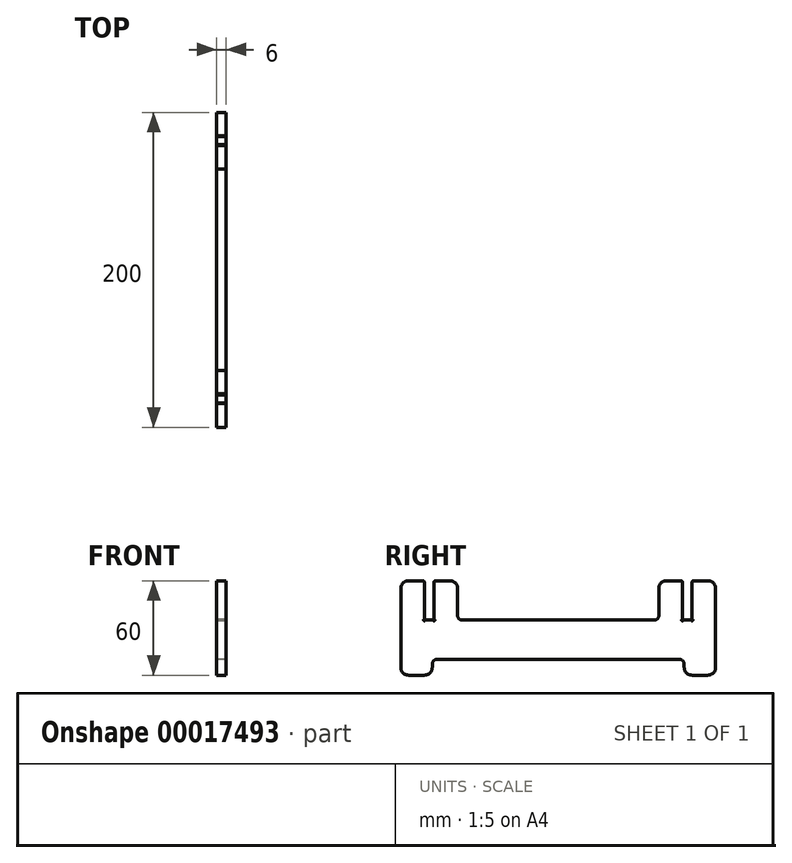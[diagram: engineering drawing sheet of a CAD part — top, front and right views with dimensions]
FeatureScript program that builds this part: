
annotation { "Feature Type Name" : "Feature", "Feature Type Description" : "" }
export const myFeature = defineFeature(function(context is Context, id is Id, definition is map)
    precondition{}
    {
        {
            var Q0;
            Q0=qCreatedBy(makeId("Right.planeOp"),FACE);
            var sketch = newSketch(context, id + "F0", { "sketchPlane" : qUnion([Q0])});
            skLineSegment(sketch, "E0.bottom", {"start": v(-95, 0) * mm, "end": v(-85, 0) * mm});
            skLineSegment(sketch, "E0.top", {"start": v(-95, 60) * mm, "end": v(-86, 60) * mm});
            skLineSegment(sketch, "E0.left", {"start": v(-100, 5) * mm, "end": v(-100, 55) * mm});
            skLineSegment(sketch, "E0.right", {"start": v(100, 5) * mm, "end": v(100, 55) * mm});
            skLineSegment(sketch, "E1", {"start": v(0, 0) * mm, "end": v(0, 136.34) * mm, "construction": true});
            skLineSegment(sketch, "E2.top", {"start": v(-77, 10) * mm, "end": v(77, 10) * mm});
            skLineSegment(sketch, "E2.left", {"start": v(-80, 5) * mm, "end": v(-80, 7) * mm});
            skLineSegment(sketch, "E2.right", {"start": v(80, 5) * mm, "end": v(80, 7) * mm});
            skLineSegment(sketch, "E3.trimOffspring", {"start": v(85, 0) * mm, "end": v(95, 0) * mm});
            skLineSegment(sketch, "E4.top", {"start": v(-84.5, 35) * mm, "end": v(-79.4, 35) * mm});
            skLineSegment(sketch, "E4.left", {"start": v(-85, 59) * mm, "end": v(-85, 35.5) * mm});
            skLineSegment(sketch, "E4.right", {"start": v(-78.9, 59) * mm, "end": v(-78.9, 35.5) * mm});
            skLineSegment(sketch, "E5.top", {"start": v(79.4, 35) * mm, "end": v(84.5, 35) * mm});
            skLineSegment(sketch, "E5.left", {"start": v(78.9, 59) * mm, "end": v(78.9, 35.5) * mm});
            skLineSegment(sketch, "E5.right", {"start": v(85, 59) * mm, "end": v(85, 35.5) * mm});
            skLineSegment(sketch, "E6.trimOffspring", {"start": v(-77.9, 60) * mm, "end": v(-68.9, 60) * mm});
            skLineSegment(sketch, "E7.trimOffspring", {"start": v(86, 60) * mm, "end": v(95, 60) * mm});
            skArc(sketch, "E8", {"start": v(-85, 35.5) * mm, "mid": v(-85.35, 34.65) * mm, "end": v(-84.5, 35) * mm});
            skArc(sketch, "E9", {"start": v(-79.4, 35) * mm, "mid": v(-78.55, 34.65) * mm, "end": v(-78.9, 35.5) * mm});
            skArc(sketch, "E10", {"start": v(78.9, 35.5) * mm, "mid": v(78.55, 34.65) * mm, "end": v(79.4, 35) * mm});
            skArc(sketch, "E11", {"start": v(84.5, 35) * mm, "mid": v(85.35, 34.65) * mm, "end": v(85, 35.5) * mm});
            skPoint(sketch, "E12.visualSharp", {"position": v(-85, 60) * mm});
            skArc(sketch, "E12.filletArc", {"start": v(-85, 59) * mm, "mid": v(-85.3, 59.7) * mm, "end": v(-86, 60) * mm});
            skPoint(sketch, "E13.visualSharp", {"position": v(-78.9, 60) * mm});
            skArc(sketch, "E13.filletArc", {"start": v(-77.9, 60) * mm, "mid": v(-78.6, 59.7) * mm, "end": v(-78.9, 59) * mm});
            skPoint(sketch, "E14.visualSharp", {"position": v(78.9, 60) * mm});
            skArc(sketch, "E14.filletArc", {"start": v(78.9, 59) * mm, "mid": v(78.6, 59.7) * mm, "end": v(77.9, 60) * mm});
            skPoint(sketch, "E15.visualSharp", {"position": v(85, 60) * mm});
            skArc(sketch, "E15.filletArc", {"start": v(86, 60) * mm, "mid": v(85.3, 59.7) * mm, "end": v(85, 59) * mm});
            skPoint(sketch, "E16.visualSharp", {"position": v(-100, 60) * mm});
            skArc(sketch, "E16.filletArc", {"start": v(-95, 60) * mm, "mid": v(-98.54, 58.54) * mm, "end": v(-100, 55) * mm});
            skPoint(sketch, "E17.visualSharp", {"position": v(100, 60) * mm});
            skArc(sketch, "E17.filletArc", {"start": v(100, 55) * mm, "mid": v(98.54, 58.54) * mm, "end": v(95, 60) * mm});
            skPoint(sketch, "E18.visualSharp", {"position": v(-100, 0) * mm});
            skArc(sketch, "E18.filletArc", {"start": v(-100, 5) * mm, "mid": v(-98.54, 1.46) * mm, "end": v(-95, 0) * mm});
            skPoint(sketch, "E19.visualSharp", {"position": v(-80, 0) * mm});
            skArc(sketch, "E19.filletArc", {"start": v(-85, 0) * mm, "mid": v(-81.46, 1.46) * mm, "end": v(-80, 5) * mm});
            skPoint(sketch, "E20.visualSharp", {"position": v(80, 0) * mm});
            skArc(sketch, "E20.filletArc", {"start": v(80, 5) * mm, "mid": v(81.46, 1.46) * mm, "end": v(85, 0) * mm});
            skPoint(sketch, "E21.visualSharp", {"position": v(100, 0) * mm});
            skArc(sketch, "E21.filletArc", {"start": v(95, 0) * mm, "mid": v(98.54, 1.46) * mm, "end": v(100, 5) * mm});
            skPoint(sketch, "E22.visualSharp", {"position": v(-80, 10) * mm});
            skArc(sketch, "E22.filletArc", {"start": v(-77, 10) * mm, "mid": v(-79.12, 9.12) * mm, "end": v(-80, 7) * mm});
            skPoint(sketch, "E23.visualSharp", {"position": v(80, 10) * mm});
            skArc(sketch, "E23.filletArc", {"start": v(80, 7) * mm, "mid": v(79.12, 9.12) * mm, "end": v(77, 10) * mm});
            skLineSegment(sketch, "E24.top", {"start": v(-60.9, 35) * mm, "end": v(60.9, 35) * mm});
            skLineSegment(sketch, "E24.left", {"start": v(-63.9, 55) * mm, "end": v(-63.9, 38) * mm});
            skLineSegment(sketch, "E24.right", {"start": v(63.9, 55) * mm, "end": v(63.9, 38) * mm});
            skLineSegment(sketch, "E25.trimOffspring", {"start": v(68.9, 60) * mm, "end": v(77.9, 60) * mm});
            skPoint(sketch, "E26.visualSharp", {"position": v(-63.9, 60) * mm});
            skArc(sketch, "E26.filletArc", {"start": v(-63.9, 55) * mm, "mid": v(-65.36, 58.54) * mm, "end": v(-68.9, 60) * mm});
            skPoint(sketch, "E27.visualSharp", {"position": v(63.9, 60) * mm});
            skArc(sketch, "E27.filletArc", {"start": v(68.9, 60) * mm, "mid": v(65.36, 58.54) * mm, "end": v(63.9, 55) * mm});
            skPoint(sketch, "E28.visualSharp", {"position": v(-63.9, 35) * mm});
            skArc(sketch, "E28.filletArc", {"start": v(-63.9, 38) * mm, "mid": v(-63.02, 35.88) * mm, "end": v(-60.9, 35) * mm});
            skPoint(sketch, "E29.visualSharp", {"position": v(63.9, 35) * mm});
            skArc(sketch, "E29.filletArc", {"start": v(60.9, 35) * mm, "mid": v(63.02, 35.88) * mm, "end": v(63.9, 38) * mm});
            skSolve(sketch);
        }
        {
            var Q0;
            Q0 = qSketchRegion(id + "F0", true);
            extrude(context, id + "F1", {"entities" : qUnion([Q0]), "depth" : 6 * mm});
        }
    });
